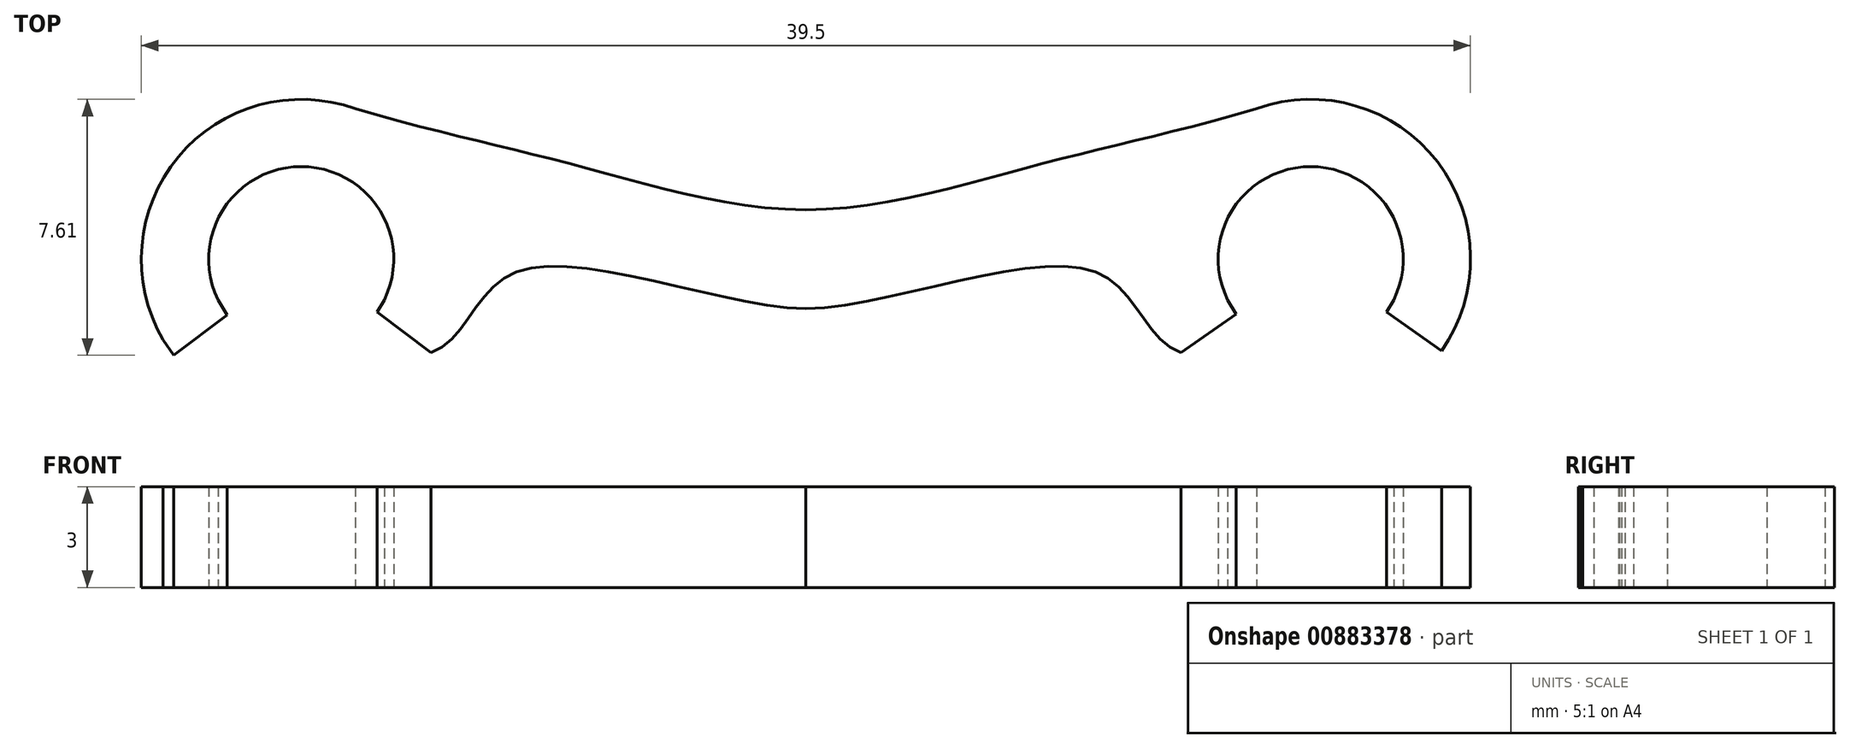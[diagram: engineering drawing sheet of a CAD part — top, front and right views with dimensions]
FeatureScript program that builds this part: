
annotation { "Feature Type Name" : "Feature", "Feature Type Description" : "" }
export const myFeature = defineFeature(function(context is Context, id is Id, definition is map)
    precondition{}
    {
        {
            var Q0;
            Q0=qCreatedBy(makeId("Top.planeOp"),FACE);
            var sketch = newSketch(context, id + "F0", { "sketchPlane" : qUnion([Q0])});
            skArc(sketch, "E0", {"start": v(-13.4, 4.47) * mm, "mid": v(-18.65, 3.04) * mm, "end": v(-19.1, -2.4) * mm});
            skFitSpline(sketch, "E1", {"points": [v(-13.4, 4.47) * mm, v(-6.8, 2.78) * mm, v(0, 1.47) * mm], "startDerivative": vector(15.64, -4.54) * mm, "endDerivative": vector(14.05, -0.03) * mm});
            skArc(sketch, "E2", {"start": v(-12.53, -1.21) * mm, "mid": v(-15, 2.75) * mm, "end": v(-17.47, -1.21) * mm});
            skLineSegment(sketch, "E3", {"start": v(-17.56, -1.93) * mm, "end": v(-18.37, -2.54) * mm, "construction": true});
            skLineSegment(sketch, "E4", {"start": v(-7.87, -5.25) * mm, "end": v(-12.38, -1.85) * mm, "construction": true});
            skLineSegment(sketch, "E5", {"start": v(-12.75, -1.58) * mm, "end": v(-11.15, -2.78) * mm});
            skLineSegment(sketch, "E6", {"start": v(-17.2, -1.65) * mm, "end": v(-18.8, -2.86) * mm});
            skFitSpline(sketch, "E7.MirrorCS", {"points": [v(13.4, 4.47) * mm, v(6.8, 2.78) * mm, v(0, 1.47) * mm], "startDerivative": vector(-15.64, -4.54) * mm, "endDerivative": vector(-14.05, -0.03) * mm});
            skArc(sketch, "E8.MirrorCS", {"start": v(13.4, 4.47) * mm, "mid": v(18.78, 2.88) * mm, "end": v(18.9, -2.72) * mm});
            skArc(sketch, "E9.MirrorCS", {"start": v(13.4, 4.47) * mm, "mid": v(18.6, 3.1) * mm, "end": v(19.18, -2.25) * mm});
            skArc(sketch, "E10.MirrorCS", {"start": v(12.53, -1.21) * mm, "mid": v(15, 2.75) * mm, "end": v(17.47, -1.21) * mm});
            skLineSegment(sketch, "E11.MirrorCS", {"start": v(15, 0) * mm, "end": v(22.43, -5.6) * mm, "construction": true});
            skLineSegment(sketch, "E12.MirrorCS", {"start": v(7.87, -5.25) * mm, "end": v(12.38, -1.85) * mm, "construction": true});
            skFitSpline(sketch, "E13", {"points": [v(-11.15, -2.78) * mm, v(-8.65, -0.4) * mm, v(0, -1.47) * mm], "startDerivative": vector(8.45, 3.1) * mm, "endDerivative": vector(12.27, -0.1) * mm});
            skPoint(sketch, "E14.MirrorCS.start.orphan", {"position": v(-13.4, -4.47) * mm});
            skPoint(sketch, "E15.MirrorCS.start.orphan", {"position": v(13.4, -4.47) * mm});
            skFitSpline(sketch, "E16.MirrorCS", {"points": [v(11.15, -2.78) * mm, v(8.65, -0.4) * mm, v(0, -1.47) * mm], "startDerivative": vector(-8.45, 3.1) * mm, "endDerivative": vector(-12.27, -0.1) * mm});
            skLineSegment(sketch, "E17.MirrorCS", {"start": v(17.56, -1.93) * mm, "end": v(18.37, -2.54) * mm, "construction": true});
            skLineSegment(sketch, "E18.MirrorCS", {"start": v(7.87, -5.25) * mm, "end": v(14.94, 0.08) * mm, "construction": true});
            skLineSegment(sketch, "E19", {"start": v(11.15, -2.78) * mm, "end": v(12.79, -1.63) * mm});
            skLineSegment(sketch, "E20", {"start": v(17.25, -1.58) * mm, "end": v(18.9, -2.72) * mm});
            skPoint(sketch, "E21.newPointA", {"position": v(-17.25, -1.58) * mm});
            skPoint(sketch, "E22.newPointA", {"position": v(-18.9, -2.72) * mm});
            skPoint(sketch, "E22.newPointB", {"position": v(-22.43, -5.6) * mm});
            skArc(sketch, "E22.filletArc", {"start": v(-19.1, -2.4) * mm, "mid": v(-19.09, -2.42) * mm, "end": v(-19.07, -2.44) * mm});
            skPoint(sketch, "E23.newPointA", {"position": v(12.75, -1.58) * mm});
            skPoint(sketch, "E23.newPointB", {"position": v(14.94, 0.08) * mm});
            skPoint(sketch, "E24.newPointA", {"position": v(17.25, -1.58) * mm});
            skPoint(sketch, "E25.newPointA", {"position": v(-12.75, -1.58) * mm});
            skPoint(sketch, "E25.newPointB", {"position": v(-14.94, 0.08) * mm});
            skPoint(sketch, "E26.newPointA", {"position": v(18.9, -2.72) * mm});
            skPoint(sketch, "E26.newPointB", {"position": v(22.43, -5.6) * mm});
            skLineSegment(sketch, "E27", {"start": v(17.47, -1.21) * mm, "end": v(17.25, -1.58) * mm});
            skLineSegment(sketch, "E28", {"start": v(12.53, -1.21) * mm, "end": v(12.79, -1.63) * mm});
            skLineSegment(sketch, "E29", {"start": v(-12.53, -1.21) * mm, "end": v(-12.75, -1.58) * mm});
            skLineSegment(sketch, "E30", {"start": v(-17.47, -1.21) * mm, "end": v(-17.2, -1.65) * mm});
            skLineSegment(sketch, "E31", {"start": v(-19.1, -2.4) * mm, "end": v(-18.8, -2.86) * mm});
            skSolve(sketch);
        }
        {
            var Q0;
            {var subQ1=sQuery(id+"F0.wireOp",EDGE,"E0");Q0=makeQuery(id+"F0.imprint","IMPRINT",FACE,{"disambiguationData":[TD([[makeQuery(id+"F0.imprint","IMPRINT",EDGE,{"derivedFrom":subQ1}),1.0]])]});}
            extrude(context, id + "F1", {"entities" : qUnion([Q0]), "depth" : 3 * mm, "offsetDistance" : 25 * mm});
        }
    });
